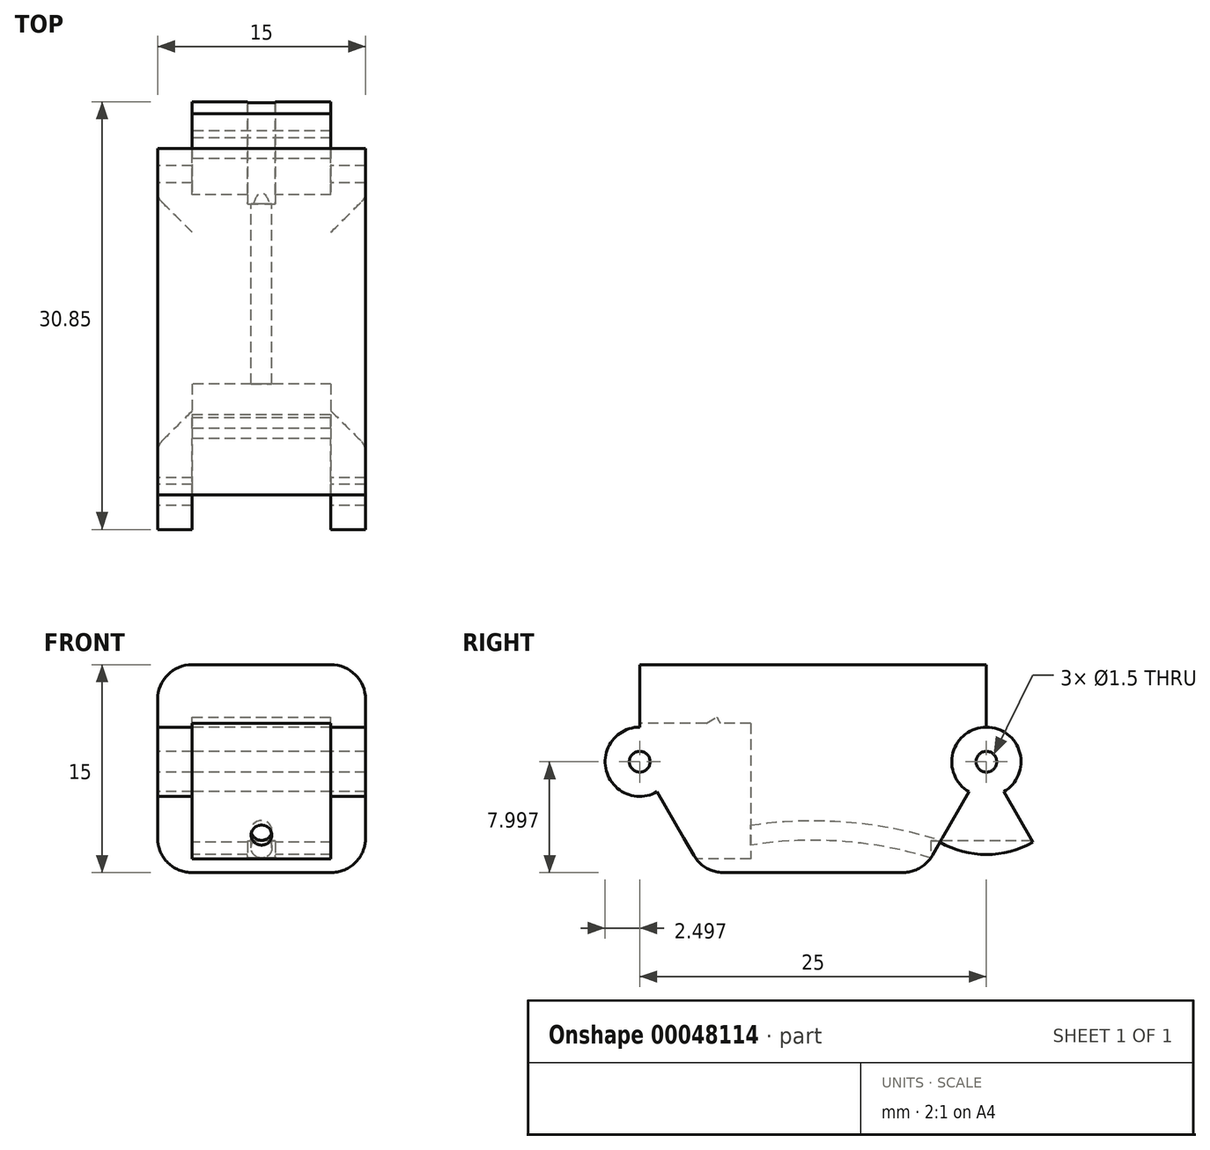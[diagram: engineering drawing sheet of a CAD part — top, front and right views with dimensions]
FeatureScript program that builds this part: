
annotation { "Feature Type Name" : "Feature", "Feature Type Description" : "" }
export const myFeature = defineFeature(function(context is Context, id is Id, definition is map)
    precondition{}
    {
        {
            var Q0;
            Q0=qCreatedBy(makeId("Right.planeOp"),FACE);
            var sketch = newSketch(context, id + "F0", { "sketchPlane" : qUnion([Q0])});
            skLineSegment(sketch, "E0.bottom", {"start": v(-42.54, 1.89) * mm, "end": v(-17.54, 1.89) * mm});
            skLineSegment(sketch, "E0.top", {"start": v(-42.54, -13.11) * mm, "end": v(-17.54, -13.11) * mm});
            skLineSegment(sketch, "E0.left", {"start": v(-42.54, 1.89) * mm, "end": v(-42.54, -13.11) * mm});
            skLineSegment(sketch, "E0.right", {"start": v(-17.54, 1.89) * mm, "end": v(-17.54, -13.11) * mm});
            skCircle(sketch, "E1", {"center": v(-17.54, -5.11) * mm, "radius": 2.5 * mm});
            skCircle(sketch, "E2", {"center": v(-17.54, -5.11) * mm, "radius": 6.7 * mm});
            skLineSegment(sketch, "E3", {"start": v(-17.54, -5.11) * mm, "end": v(-14.2, -10.91) * mm});
            skCircle(sketch, "E4", {"center": v(-17.54, -5.11) * mm, "radius": 0.75 * mm});
            skLineSegment(sketch, "E5", {"start": v(-17.54, -5.11) * mm, "end": v(-22.16, -13.11) * mm});
            skCircle(sketch, "E6", {"center": v(-42.54, -5.11) * mm, "radius": 2.5 * mm});
            skCircle(sketch, "E7", {"center": v(-42.54, -5.11) * mm, "radius": 0.75 * mm});
            skLineSegment(sketch, "E8", {"start": v(-42.54, -5.11) * mm, "end": v(-37.92, -13.11) * mm});
            skArc(sketch, "E9", {"start": v(-39.32, -10.69) * mm, "mid": v(-36.32, -6.78) * mm, "end": v(-36.97, -1.9) * mm});
            skLineSegment(sketch, "E10", {"start": v(-42.54, -5.11) * mm, "end": v(-30.42, 1.89) * mm});
            skSolve(sketch);
        }
        {
            var Q0;
            {var subQ3=sQuery(id+"F0.wireOp",EDGE,"E0.right");var subQ7=sQuery(id+"F0.wireOp",EDGE,"E0.bottom");var subQ8=makeQuery(id+"F0.imprint","INTERSECT",VERTEX,{"derivedFrom":[subQ7,subQ3]});Q0=makeQuery(id+"F0.imprint","IMPRINT",FACE,{"disambiguationData":[TD([[makeQuery(id+"F0.imprint","IMPRINT",EDGE,{"disambiguationData":[TD([[subQ8,1.0]])],"derivedFrom":subQ7}),-1.0]])]});}
            var Q1;
            {var subQ5=sQuery(id+"F0.wireOp",EDGE,"E0.left");var subQ11=sQuery(id+"F0.wireOp",EDGE,"E0.bottom");var subQ13=makeQuery(id+"F0.imprint","INTERSECT",VERTEX,{"derivedFrom":[subQ11,subQ5]});Q1=makeQuery(id+"F0.imprint","IMPRINT",FACE,{"disambiguationData":[TD([[makeQuery(id+"F0.imprint","IMPRINT",EDGE,{"disambiguationData":[TD([[subQ13,-1.0]])],"derivedFrom":subQ11}),-1.0]])]});}
            var Q2;
            {var subQ3=sQuery(id+"F0.wireOp",EDGE,"E6");var subQ5=sQuery(id+"F0.wireOp",EDGE,"E0.left");var subQ6=makeQuery(id+"F0.imprint","INTERSECT",VERTEX,{"disambiguationData":[OD(1.0)],"derivedFrom":[subQ5,subQ3]});Q2=makeQuery(id+"F0.imprint","IMPRINT",FACE,{"disambiguationData":[TD([[makeQuery(id+"F0.imprint","IMPRINT",EDGE,{"disambiguationData":[TD([[subQ6,1.0]])],"derivedFrom":subQ5}),1.0]])]});}
            var Q3;
            {var subQ1=sQuery(id+"F0.wireOp",EDGE,"E0.left");var subQ4=sQuery(id+"F0.wireOp",EDGE,"E6");var subQ6=makeQuery(id+"F0.imprint","INTERSECT",VERTEX,{"disambiguationData":[OD(0.0)],"derivedFrom":[subQ1,subQ4]});Q3=makeQuery(id+"F0.imprint","IMPRINT",FACE,{"disambiguationData":[TD([[makeQuery(id+"F0.imprint","IMPRINT",EDGE,{"disambiguationData":[TD([[subQ6,-1.0]])],"derivedFrom":subQ1}),-1.0]])]});}
            var Q4;
            {var subQ3=sQuery(id+"F0.wireOp",EDGE,"E6");var subQ5=sQuery(id+"F0.wireOp",EDGE,"E0.left");var subQ7=makeQuery(id+"F0.imprint","INTERSECT",VERTEX,{"disambiguationData":[OD(0.0)],"derivedFrom":[subQ5,subQ3]});Q4=makeQuery(id+"F0.imprint","IMPRINT",FACE,{"disambiguationData":[TD([[makeQuery(id+"F0.imprint","IMPRINT",EDGE,{"disambiguationData":[TD([[subQ7,-1.0]])],"derivedFrom":subQ5}),1.0]])]});}
            var Q5;
            {var subQ0=sQuery(id+"F0.wireOp",EDGE,"E9");Q5=makeQuery(id+"F0.imprint","IMPRINT",FACE,{"disambiguationData":[TD([[makeQuery(id+"F0.imprint","IMPRINT",EDGE,{"derivedFrom":subQ0}),-1.0]])]});}
            var Q6;
            {var subQ3=sQuery(id+"F0.wireOp",EDGE,"E9");Q6=makeQuery(id+"F0.imprint","IMPRINT",FACE,{"disambiguationData":[TD([[makeQuery(id+"F0.imprint","IMPRINT",EDGE,{"derivedFrom":subQ3}),1.0]])]});}
            var Q7;
            {var subQ0=sQuery(id+"F0.wireOp",EDGE,"E10");var subQ3=sQuery(id+"F0.wireOp",EDGE,"E6");var subQ4=makeQuery(id+"F0.imprint","INTERSECT",VERTEX,{"derivedFrom":[subQ3,subQ0]});Q7=makeQuery(id+"F0.imprint","IMPRINT",FACE,{"disambiguationData":[TD([[makeQuery(id+"F0.imprint","IMPRINT",EDGE,{"disambiguationData":[TD([[subQ4,1.0]])],"derivedFrom":subQ3}),1.0]])]});}
            var Q8;
            {var subQ0=sQuery(id+"F0.wireOp",EDGE,"E2");var subQ1=sQuery(id+"F0.wireOp",EDGE,"E0.right");var subQ2=makeQuery(id+"F0.imprint","INTERSECT",VERTEX,{"disambiguationData":[OD(0.0)],"derivedFrom":[subQ1,subQ0]});Q8=makeQuery(id+"F0.imprint","IMPRINT",FACE,{"disambiguationData":[TD([[makeQuery(id+"F0.imprint","IMPRINT",EDGE,{"disambiguationData":[TD([[subQ2,-1.0]])],"derivedFrom":subQ1}),-1.0]])]});}
            extrude(context, id + "F1", {"entities" : qUnion([Q0, Q1, Q2, Q3, Q4, Q5, Q6, Q7, Q8]), "depth" : 15 * mm, "symmetric" : true});
        }
        {
            var Q0;
            {var subQ3=sQuery(id+"F0.wireOp",EDGE,"E1");var subQ5=sQuery(id+"F0.wireOp",EDGE,"E0.right");var subQ6=makeQuery(id+"F0.imprint","INTERSECT",VERTEX,{"disambiguationData":[OD(0.0)],"derivedFrom":[subQ5,subQ3]});Q0=makeQuery(id+"F0.imprint","IMPRINT",FACE,{"disambiguationData":[TD([[makeQuery(id+"F0.imprint","IMPRINT",EDGE,{"disambiguationData":[TD([[subQ6,-1.0]])],"derivedFrom":subQ5}),-1.0]])]});}
            var Q1;
            {var subQ3=sQuery(id+"F0.wireOp",EDGE,"E0.right");var subQ5=sQuery(id+"F0.wireOp",EDGE,"E1");var subQ7=makeQuery(id+"F0.imprint","INTERSECT",VERTEX,{"disambiguationData":[OD(0.0)],"derivedFrom":[subQ3,subQ5]});Q1=makeQuery(id+"F0.imprint","IMPRINT",FACE,{"disambiguationData":[TD([[makeQuery(id+"F0.imprint","IMPRINT",EDGE,{"disambiguationData":[TD([[subQ7,-1.0]])],"derivedFrom":subQ3}),1.0]])]});}
            var Q2;
            {var subQ1=sQuery(id+"F0.wireOp",EDGE,"E4");var subQ5=sQuery(id+"F0.wireOp",EDGE,"E0.right");var subQ7=makeQuery(id+"F0.imprint","INTERSECT",VERTEX,{"disambiguationData":[OD(1.0)],"derivedFrom":[subQ5,subQ1]});Q2=makeQuery(id+"F0.imprint","IMPRINT",FACE,{"disambiguationData":[TD([[makeQuery(id+"F0.imprint","IMPRINT",EDGE,{"disambiguationData":[TD([[subQ7,-1.0]])],"derivedFrom":subQ5}),1.0]])]});}
            var Q3;
            {var subQ0=sQuery(id+"F0.wireOp",EDGE,"E4");var subQ3=sQuery(id+"F0.wireOp",EDGE,"E0.right");var subQ4=makeQuery(id+"F0.imprint","INTERSECT",VERTEX,{"disambiguationData":[OD(1.0)],"derivedFrom":[subQ3,subQ0]});Q3=makeQuery(id+"F0.imprint","IMPRINT",FACE,{"disambiguationData":[TD([[makeQuery(id+"F0.imprint","IMPRINT",EDGE,{"disambiguationData":[TD([[subQ4,-1.0]])],"derivedFrom":subQ3}),-1.0]])]});}
            var Q4;
            {var subQ3=sQuery(id+"F0.wireOp",EDGE,"E0.right");var subQ5=sQuery(id+"F0.wireOp",EDGE,"E1");var subQ7=makeQuery(id+"F0.imprint","INTERSECT",VERTEX,{"disambiguationData":[OD(1.0)],"derivedFrom":[subQ3,subQ5]});Q4=makeQuery(id+"F0.imprint","IMPRINT",FACE,{"disambiguationData":[TD([[makeQuery(id+"F0.imprint","IMPRINT",EDGE,{"disambiguationData":[TD([[subQ7,1.0]])],"derivedFrom":subQ5}),-1.0]])]});}
            var Q5;
            {var subQ1=sQuery(id+"F0.wireOp",EDGE,"E1");var subQ5=sQuery(id+"F0.wireOp",EDGE,"E0.right");var subQ7=makeQuery(id+"F0.imprint","INTERSECT",VERTEX,{"disambiguationData":[OD(1.0)],"derivedFrom":[subQ5,subQ1]});Q5=makeQuery(id+"F0.imprint","IMPRINT",FACE,{"disambiguationData":[TD([[makeQuery(id+"F0.imprint","IMPRINT",EDGE,{"disambiguationData":[TD([[subQ7,-1.0]])],"derivedFrom":subQ1}),-1.0]])]});}
            extrude(context, id + "F2", {"entities" : qUnion([Q0, Q1, Q2, Q3, Q4, Q5]), "operationType" : NewBodyOperationType.ADD, "depth" : 10 * mm, "symmetric" : true});
        }
        {
            var Q0;
            Q0=qCreatedBy(makeId("Right.planeOp"),FACE);
            var sketch = newSketch(context, id + "F3", { "sketchPlane" : qUnion([Q0])});
            skCircle(sketch, "E11", {"center": v(-42.54, -5.11) * mm, "radius": 2.7 * mm});
            skSolve(sketch);
        }
        {
            var Q0;
            Q0=qSketchRegion(id+"F3",true);
            extrude(context, id + "F4", {"entities" : qUnion([Q0]), "operationType" : NewBodyOperationType.REMOVE, "oppositeDirection" : true, "depth" : 10 * mm, "symmetric" : true});
        }
        {
            var Q0;
            {var subQ0=sQuery(id+"F0.wireOp",EDGE,"E0.left");Q0=makeQuery(id+"F1.opExtrude","SWEPT_FACE",FACE,{"disambiguationData":[OSD([subQ0]),TDD([makeQuery(id+"F0.imprint","IMPRINT",EDGE,{"disambiguationData":[TD([[makeQuery(id+"F0.imprint","INTERSECT",VERTEX,{"derivedFrom":[sQuery(id+"F0.wireOp",EDGE,"E0.bottom"),subQ0]}),-1.0]])],"derivedFrom":subQ0})])]});}
            var sketch = newSketch(context, id + "F5", { "sketchPlane" : qUnion([Q0])});
            skLineSegment(sketch, "E12.bottom", {"start": v(5, -2.35) * mm, "end": v(-5, -2.35) * mm});
            skLineSegment(sketch, "E12.top", {"start": v(5, -12.11) * mm, "end": v(-5, -12.11) * mm});
            skLineSegment(sketch, "E12.left", {"start": v(5, -2.35) * mm, "end": v(5, -12.11) * mm});
            skLineSegment(sketch, "E12.right", {"start": v(-5, -2.35) * mm, "end": v(-5, -12.11) * mm});
            skSolve(sketch);
        }
        {
            var Q0;
            Q0=qSketchRegion(id+"F5",true);
            extrude(context, id + "F6", {"entities" : qUnion([Q0]), "operationType" : NewBodyOperationType.REMOVE, "oppositeDirection" : true, "depth" : 8 * mm});
        }
        {
            var Q0;
            {var subQ3=sQuery(id+"F0.wireOp",EDGE,"E9");Q0=makeQuery(id+"F0.imprint","IMPRINT",FACE,{"disambiguationData":[TD([[makeQuery(id+"F0.imprint","IMPRINT",EDGE,{"derivedFrom":subQ3}),1.0]])]});}
            extrude(context, id + "F7", {"entities" : qUnion([Q0]), "operationType" : NewBodyOperationType.REMOVE, "oppositeDirection" : true, "depth" : 10 * mm, "symmetric" : true});
        }
        {
            var Q0;
            Q0=makeQuery(id+"F1.opExtrude","SWEPT_FACE",FACE,{"disambiguationData":[OSD([sQuery(id+"F0.wireOp",EDGE,"E0.top")])]});
            var sketch = newSketch(context, id + "F8", { "sketchPlane" : qUnion([Q0])});
            skLineSegment(sketch, "E13.rect.bottom", {"start": v(-1, 13.54) * mm, "end": v(1, 13.54) * mm});
            skLineSegment(sketch, "E13.rect.top", {"start": v(-1, 21.54) * mm, "end": v(1, 21.54) * mm});
            skLineSegment(sketch, "E13.rect.left", {"start": v(-1, 13.54) * mm, "end": v(-1, 21.54) * mm});
            skLineSegment(sketch, "E13.rect.right", {"start": v(1, 13.54) * mm, "end": v(1, 21.54) * mm});
            skPoint(sketch, "E13.rect.middle", {"position": v(0, 17.54) * mm});
            skSolve(sketch);
        }
        {
            var Q0;
            Q0=qSketchRegion(id+"F8",true);
            extrude(context, id + "F9", {"entities" : qUnion([Q0]), "operationType" : NewBodyOperationType.REMOVE, "oppositeDirection" : true, "depth" : 2.3 * mm});
        }
        {
            var Q0;
            Q0=makeQuery(id+"F6.boolean.opBoolean","COPY",FACE,{"derivedFrom":makeQuery(id+"F6.opExtrude","CAP_FACE",FACE,{"disambiguationData":[OSD([sQuery(id+"F5.wireOp",EDGE,"E12.bottom"),sQuery(id+"F5.wireOp",EDGE,"E12.top"),sQuery(id+"F5.wireOp",EDGE,"E12.left"),sQuery(id+"F5.wireOp",EDGE,"E12.right")])],"isStart":false})});
            cPlane(context, id + "F10", {"entities" : qUnion([Q0]), "cplaneType" : CPlaneType.OFFSET, "offset" : 4.54 * mm, "width" : 150 * mm, "height" : 150 * mm});
        }
        {
            var Q0;
            Q0=qCreatedBy(id+"F10.planeOp",FACE);
            var sketch = newSketch(context, id + "F11", { "sketchPlane" : qUnion([Q0])});
            skCircle(sketch, "E14", {"center": v(0, -11.47) * mm, "radius": 0.75 * mm});
            skPoint(sketch, "E15", {"position": v(0, -12.11) * mm});
            skPoint(sketch, "E16", {"position": v(0, -13.1) * mm});
            skSolve(sketch);
        }
        {
            var Q0;
            Q0=qCreatedBy(makeId("Right.planeOp"),FACE);
            var sketch = newSketch(context, id + "F12", { "sketchPlane" : qUnion([Q0])});
            skArc(sketch, "E17", {"start": v(-21.05, -11.47) * mm, "mid": v(-30.07, -10.07) * mm, "end": v(-39.08, -11.47) * mm});
            skSolve(sketch);
        }
        {
            var Q0;
            Q0=qSketchRegion(id+"F11",true);
            var Q1;
            Q1=qConstructionFilter(qBodyType(qCreatedBy(id+"F12",EDGE),BodyType.WIRE),ConstructionObject.NO);
            sweep(context, id + "F13", {"operationType" : NewBodyOperationType.REMOVE, "profiles" : qUnion([Q0]), "path" : qUnion([Q1])});
        }
        {
            var Q0;
            Q0=makeQuery(id+"F1.opExtrude","CAP_EDGE",EDGE,{"disambiguationData":[OSD([sQuery(id+"F0.wireOp",EDGE,"E0.bottom")])],"isStart":false});
            var Q1;
            Q1=makeQuery(id+"F1.opExtrude","CAP_EDGE",EDGE,{"disambiguationData":[OSD([sQuery(id+"F0.wireOp",EDGE,"E0.top")])],"isStart":false});
            var Q2;
            Q2=makeQuery(id+"F1.opExtrude","CAP_EDGE",EDGE,{"disambiguationData":[OSD([sQuery(id+"F0.wireOp",EDGE,"E0.bottom")])],"isStart":true});
            var Q3;
            Q3=makeQuery(id+"F1.opExtrude","CAP_EDGE",EDGE,{"disambiguationData":[OSD([sQuery(id+"F0.wireOp",EDGE,"E0.top")])],"isStart":true});
            var Q4;
            Q4=makeQuery(id+"F1.opExtrude","SWEPT_EDGE",EDGE,{"disambiguationData":[OSD([sQuery(id+"F0.wireOp",EDGE,"E0.top"),sQuery(id+"F0.wireOp",EDGE,"E5")])]});
            var Q5;
            Q5=makeQuery(id+"F1.opExtrude","SWEPT_EDGE",EDGE,{"disambiguationData":[OSD([sQuery(id+"F0.wireOp",EDGE,"E0.top"),sQuery(id+"F0.wireOp",EDGE,"E8")])]});
            fillet(context, id + "F14", {"entities" : qUnion([Q0, Q1, Q2, Q3, Q4, Q5]), "radius" : 2.5 * mm, "tangentPropagation" : true, "allowEdgeOverflow" : false});
        }
    });
